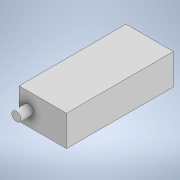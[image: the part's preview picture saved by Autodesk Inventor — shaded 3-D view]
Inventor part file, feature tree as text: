
AUTODESK INVENTOR PART (.ipt)
format: ipt  version: 2022 (Build 260153000, 153)  size: 102,400 bytes
history: native  units: mm
features: extrude x2, sketch x2
ambient origin geometry x8: Origin, YZ Plane, XZ Plane, XY Plane, X Axis, Y Axis, Z Axis, Center Point
bodies: Solid1 (feature_tree)
feature tree (4):
  extrude  "Extrusion1"  Depth=115.0mm
  extrude  "Extrusion2"  Depth=13.4mm
  sketch  "Sketch1"  dims[d0=51.0mm d1=115.0mm]
  sketch  "Sketch2"  dims[d2=33.0mm d3=0.0mm d4=10.5mm d5=9.75mm d6=13.4mm d7=0.0mm]
